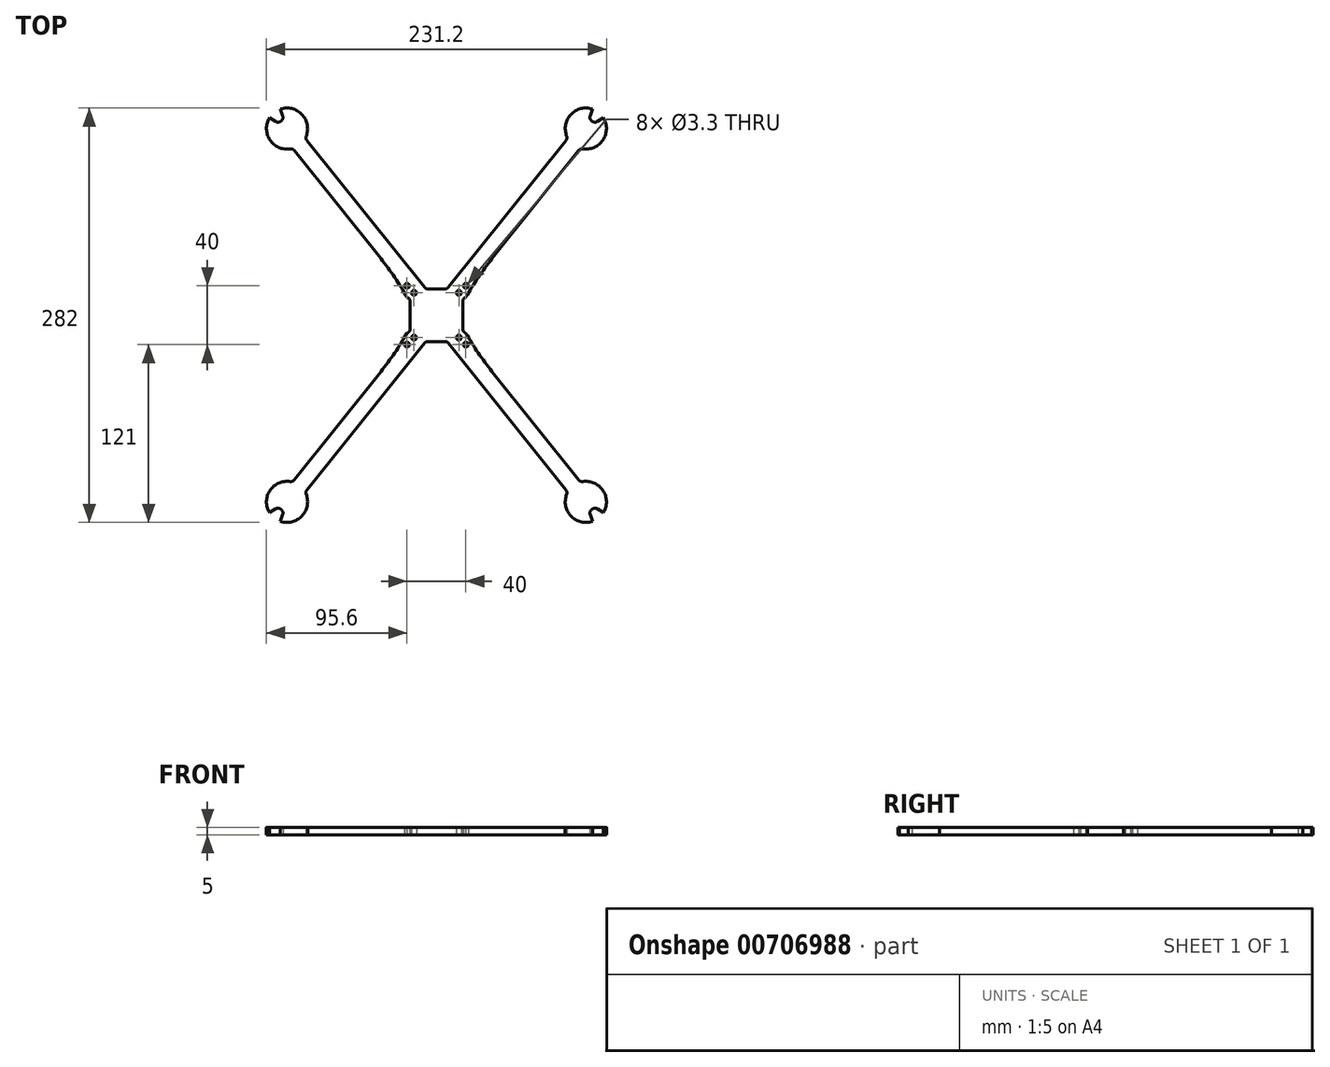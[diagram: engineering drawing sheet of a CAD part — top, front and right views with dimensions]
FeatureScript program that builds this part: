
annotation { "Feature Type Name" : "Feature", "Feature Type Description" : "" }
export const myFeature = defineFeature(function(context is Context, id is Id, definition is map)
    precondition{}
    {
        {
            var Q0;
            Q0=qCreatedBy(makeId("Top.planeOp"),FACE);
            var sketch = newSketch(context, id + "F0", { "sketchPlane" : qUnion([Q0])});
            skCircle(sketch, "E0", {"center": v(15.25, 15.25) * mm, "radius": 1.65 * mm});
            skLineSegment(sketch, "E1", {"start": v(14.09, 0) * mm, "end": v(0, 0) * mm});
            skLineSegment(sketch, "E2", {"start": v(0, 0) * mm, "end": v(101.6, 127) * mm, "construction": true});
            skCircle(sketch, "E3", {"center": v(101.6, 127) * mm, "radius": 76.2 * mm, "construction": true});
            skArc(sketch, "E4", {"start": v(106.08, 140.26) * mm, "mid": v(92.85, 116.07) * mm, "end": v(113.56, 134.28) * mm});
            skLineSegment(sketch, "E5", {"start": v(7.04, 0) * mm, "end": v(17.93, 13.6) * mm});
            skLineSegment(sketch, "E6", {"start": v(89.26, 120.38) * mm, "end": v(0, 8.8) * mm});
            skLineSegment(sketch, "E7.bottom", {"start": v(0, 0) * mm, "end": v(17.93, 0) * mm});
            skLineSegment(sketch, "E7.top", {"start": v(0, 17.93) * mm, "end": v(17.93, 17.93) * mm});
            skLineSegment(sketch, "E7.left", {"start": v(0, 0) * mm, "end": v(0, 17.93) * mm});
            skLineSegment(sketch, "E7.right", {"start": v(17.93, 0) * mm, "end": v(17.93, 17.93) * mm});
            skLineSegment(sketch, "E8", {"start": v(107.58, 130.64) * mm, "end": v(113.56, 134.28) * mm});
            skLineSegment(sketch, "E9", {"start": v(103.84, 133.63) * mm, "end": v(106.08, 140.26) * mm});
            skLineSegment(sketch, "E10", {"start": v(103.84, 133.63) * mm, "end": v(107.58, 130.64) * mm});
            skLineSegment(sketch, "E11.bottom", {"start": v(0, 0) * mm, "end": v(20, 0) * mm, "construction": true});
            skLineSegment(sketch, "E11.top", {"start": v(0, 20) * mm, "end": v(20, 20) * mm, "construction": true});
            skLineSegment(sketch, "E11.left", {"start": v(0, 0) * mm, "end": v(0, 20) * mm, "construction": true});
            skLineSegment(sketch, "E11.right", {"start": v(20, 0) * mm, "end": v(20, 20) * mm, "construction": true});
            skCircle(sketch, "E12", {"center": v(20, 20) * mm, "radius": 1.65 * mm});
            skLineSegment(sketch, "E13", {"start": v(23.32, 20.35) * mm, "end": v(20, 12.18) * mm});
            skLineSegment(sketch, "E14", {"start": v(20, 12.18) * mm, "end": v(17.93, 12.18) * mm});
            skLineSegment(sketch, "E15.trimOffspring", {"start": v(23.32, 20.35) * mm, "end": v(97.85, 113.51) * mm});
            skSolve(sketch);
        }
        {
            var Q0;
            Q0=qSketchRegion(id+"F0",true);
            extrude(context, id + "F1", {"entities" : qUnion([Q0]), "depth" : 5 * mm, "offsetDistance" : 25 * mm});
        }
        {
            var Q0;
            Q0=makeQuery(id+"F1.opExtrude","SWEPT_EDGE",EDGE,{"disambiguationData":[OSD([sQuery(id+"F0.wireOp",EDGE,"E6"),sQuery(id+"F0.wireOp",EDGE,"E7.top")])]});
            var Q1;
            Q1=makeQuery(id+"F1.opExtrude","SWEPT_EDGE",EDGE,{"disambiguationData":[OSD([sQuery(id+"F0.wireOp",EDGE,"E7.right"),sQuery(id+"F0.wireOp",EDGE,"E14")])]});
            var Q2;
            Q2=makeQuery(id+"F1.opExtrude","SWEPT_EDGE",EDGE,{"disambiguationData":[OSD([sQuery(id+"F0.wireOp",EDGE,"E4"),sQuery(id+"F0.wireOp",EDGE,"E15.trimOffspring")])]});
            var Q3;
            Q3=makeQuery(id+"F1.opExtrude","SWEPT_EDGE",EDGE,{"disambiguationData":[OSD([sQuery(id+"F0.wireOp",EDGE,"E4"),sQuery(id+"F0.wireOp",EDGE,"E6")])]});
            var Q4;
            Q4=makeQuery(id+"F1.opExtrude","SWEPT_EDGE",EDGE,{"disambiguationData":[OSD([sQuery(id+"F0.wireOp",EDGE,"E9"),sQuery(id+"F0.wireOp",EDGE,"E10")])]});
            var Q5;
            Q5=makeQuery(id+"F1.opExtrude","SWEPT_EDGE",EDGE,{"disambiguationData":[OSD([sQuery(id+"F0.wireOp",EDGE,"E8"),sQuery(id+"F0.wireOp",EDGE,"E10")])]});
            fillet(context, id + "F2", {"entities" : qUnion([Q0, Q1, Q2, Q3, Q4, Q5]), "radius" : 3 * mm, "tangentPropagation" : true, "allowEdgeOverflow" : false});
        }
        {
            var Q0;
            Q0=makeQuery(id+"F1.opExtrude","SWEPT_EDGE",EDGE,{"disambiguationData":[OSD([sQuery(id+"F0.wireOp",EDGE,"E13"),sQuery(id+"F0.wireOp",EDGE,"E15.trimOffspring")])]});
            fillet(context, id + "F3", {"entities" : qUnion([Q0]), "radius" : 199.92 * mm, "tangentPropagation" : true, "allowEdgeOverflow" : false});
        }
        {
            var Q0;
            Q0=makeQuery(id+"F1.opExtrude","SWEPT_BODY",BODY,{"disambiguationData":[OSD([sQuery(id+"F0.wireOp",EDGE,"E0"),sQuery(id+"F0.wireOp",EDGE,"E4"),sQuery(id+"F0.wireOp",EDGE,"E6"),sQuery(id+"F0.wireOp",EDGE,"E7.bottom"),sQuery(id+"F0.wireOp",EDGE,"E7.top"),sQuery(id+"F0.wireOp",EDGE,"E7.left"),sQuery(id+"F0.wireOp",EDGE,"E7.right"),sQuery(id+"F0.wireOp",EDGE,"E8"),sQuery(id+"F0.wireOp",EDGE,"E9"),sQuery(id+"F0.wireOp",EDGE,"E10"),sQuery(id+"F0.wireOp",EDGE,"E12"),sQuery(id+"F0.wireOp",EDGE,"E13"),sQuery(id+"F0.wireOp",EDGE,"E14"),sQuery(id+"F0.wireOp",EDGE,"E15.trimOffspring")])]});
            var Q1;
            Q1=qCreatedBy(makeId("Right.planeOp"),FACE);
            mirror(context, id + "F4", {"operationType" : NewBodyOperationType.ADD, "entities" : qUnion([Q0]), "mirrorPlane" : qUnion([Q1])});
        }
        {
            var Q0;
            Q0=makeQuery(id+"F1.opExtrude","SWEPT_BODY",BODY,{"disambiguationData":[OSD([sQuery(id+"F0.wireOp",EDGE,"E0"),sQuery(id+"F0.wireOp",EDGE,"E4"),sQuery(id+"F0.wireOp",EDGE,"E6"),sQuery(id+"F0.wireOp",EDGE,"E7.bottom"),sQuery(id+"F0.wireOp",EDGE,"E7.top"),sQuery(id+"F0.wireOp",EDGE,"E7.left"),sQuery(id+"F0.wireOp",EDGE,"E7.right"),sQuery(id+"F0.wireOp",EDGE,"E8"),sQuery(id+"F0.wireOp",EDGE,"E9"),sQuery(id+"F0.wireOp",EDGE,"E10"),sQuery(id+"F0.wireOp",EDGE,"E12"),sQuery(id+"F0.wireOp",EDGE,"E13"),sQuery(id+"F0.wireOp",EDGE,"E14"),sQuery(id+"F0.wireOp",EDGE,"E15.trimOffspring")])]});
            var Q1;
            Q1=qCreatedBy(makeId("Front.planeOp"),FACE);
            mirror(context, id + "F5", {"operationType" : NewBodyOperationType.ADD, "entities" : qUnion([Q0]), "mirrorPlane" : qUnion([Q1])});
        }
    });
